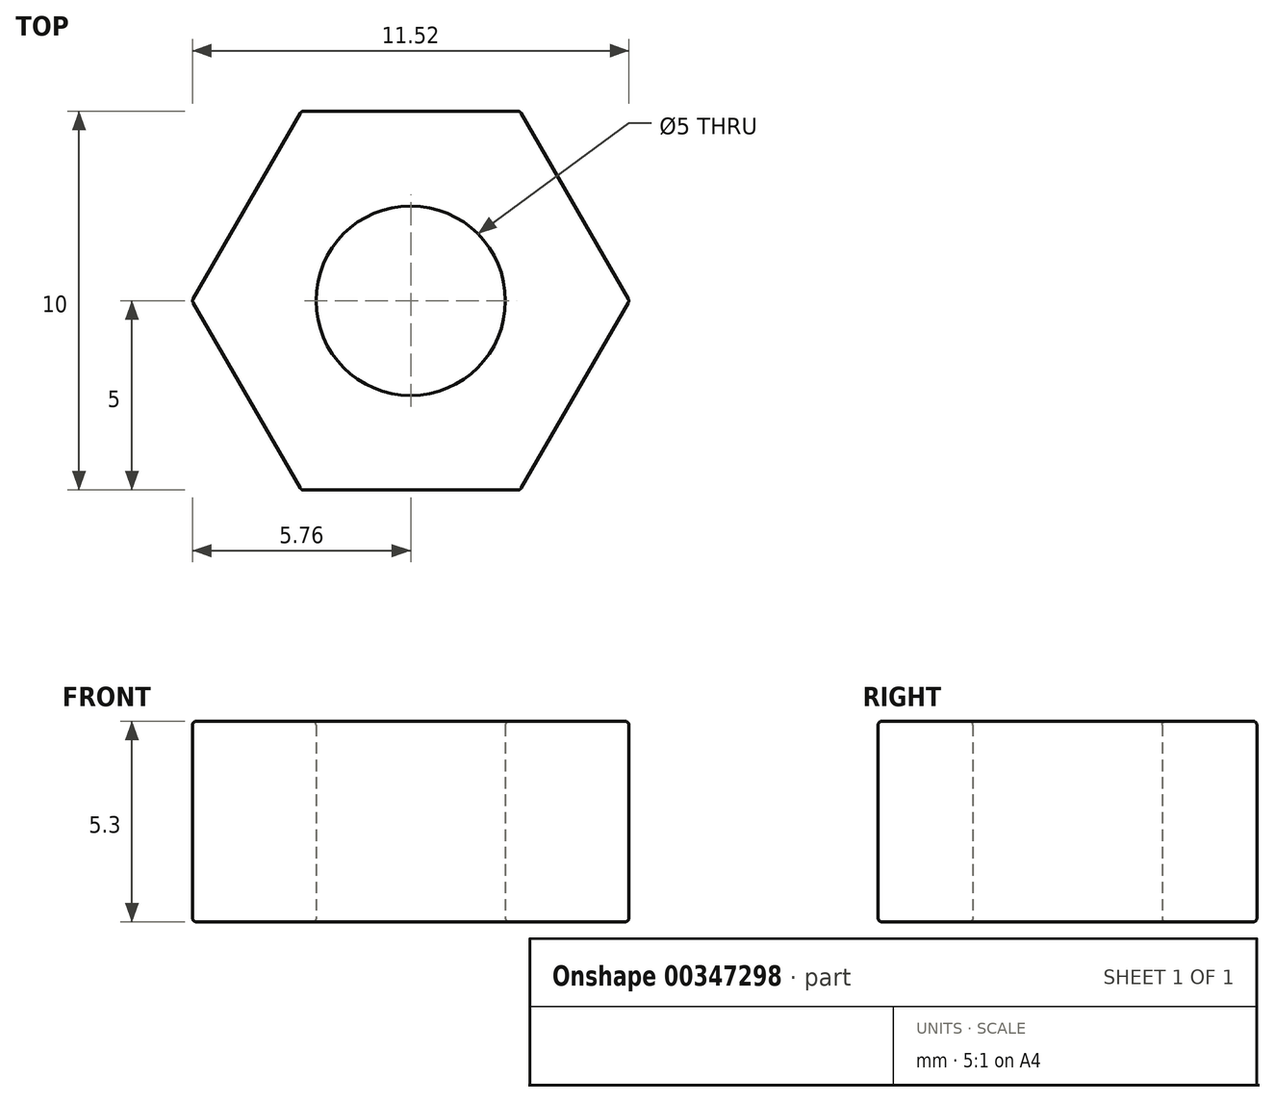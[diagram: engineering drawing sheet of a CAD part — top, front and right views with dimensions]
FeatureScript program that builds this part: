
annotation { "Feature Type Name" : "Feature", "Feature Type Description" : "" }
export const myFeature = defineFeature(function(context is Context, id is Id, definition is map)
    precondition{}
    {
        {
            var Q0;
            Q0=qCreatedBy(makeId("Top.planeOp"),FACE);
            var sketch = newSketch(context, id + "F0", { "sketchPlane" : qUnion([Q0])});
            skCircle(sketch, "E0.cCircle", {"center": v(0, 0) * mm, "radius": 5 * mm, "construction": true});
            skLineSegment(sketch, "E0.0", {"start": v(2.89, 5) * mm, "end": v(5.77, 0) * mm});
            skLineSegment(sketch, "E0.1", {"start": v(5.77, 0) * mm, "end": v(2.89, -5) * mm});
            skLineSegment(sketch, "E0.2", {"start": v(2.89, -5) * mm, "end": v(-2.89, -5) * mm});
            skLineSegment(sketch, "E0.3", {"start": v(-2.89, -5) * mm, "end": v(-5.77, 0) * mm});
            skLineSegment(sketch, "E0.4", {"start": v(-5.77, 0) * mm, "end": v(-2.89, 5) * mm});
            skLineSegment(sketch, "E0.5", {"start": v(-2.89, 5) * mm, "end": v(2.89, 5) * mm});
            skPoint(sketch, "E0.0.midPoint", {"position": v(4.33, 2.5) * mm});
            skCircle(sketch, "E1", {"center": v(0, 0) * mm, "radius": 2.5 * mm});
            skSolve(sketch);
        }
        {
            var Q0;
            Q0 = qSketchRegion(id + "F0", true);
            extrude(context, id + "F1", {"entities" : qUnion([Q0]), "depth" : 5.3 * mm});
        }
        {
            var Q0;
            Q0=makeQuery(id+"F1.opExtrude","SWEPT_FACE",FACE,{"disambiguationData":[OSD([sQuery(id+"F0.wireOp",EDGE,"E0.0")])]});
            var Q1;
            Q1=makeQuery(id+"F1.opExtrude","SWEPT_FACE",FACE,{"disambiguationData":[OSD([sQuery(id+"F0.wireOp",EDGE,"E0.1")])]});
            var Q2;
            Q2=makeQuery(id+"F1.opExtrude","CAP_FACE",FACE,{"disambiguationData":[OSD([sQuery(id+"F0.wireOp",EDGE,"E0.0"),sQuery(id+"F0.wireOp",EDGE,"E0.1"),sQuery(id+"F0.wireOp",EDGE,"E0.2"),sQuery(id+"F0.wireOp",EDGE,"E0.3"),sQuery(id+"F0.wireOp",EDGE,"E0.4"),sQuery(id+"F0.wireOp",EDGE,"E0.5"),sQuery(id+"F0.wireOp",EDGE,"E1")])],"isStart":false});
            var Q3;
            Q3=makeQuery(id+"F1.opExtrude","SWEPT_FACE",FACE,{"disambiguationData":[OSD([sQuery(id+"F0.wireOp",EDGE,"E0.2")])]});
            var Q4;
            Q4=makeQuery(id+"F1.opExtrude","CAP_FACE",FACE,{"disambiguationData":[OSD([sQuery(id+"F0.wireOp",EDGE,"E0.0"),sQuery(id+"F0.wireOp",EDGE,"E0.1"),sQuery(id+"F0.wireOp",EDGE,"E0.2"),sQuery(id+"F0.wireOp",EDGE,"E0.3"),sQuery(id+"F0.wireOp",EDGE,"E0.4"),sQuery(id+"F0.wireOp",EDGE,"E0.5"),sQuery(id+"F0.wireOp",EDGE,"E1")])],"isStart":true});
            var Q5;
            Q5=makeQuery(id+"F1.opExtrude","SWEPT_EDGE",EDGE,{"disambiguationData":[OSD([sQuery(id+"F0.wireOp",EDGE,"E0.4"),sQuery(id+"F0.wireOp",EDGE,"E0.5")])]});
            var Q6;
            Q6=makeQuery(id+"F1.opExtrude","SWEPT_FACE",FACE,{"disambiguationData":[OSD([sQuery(id+"F0.wireOp",EDGE,"E0.3")])]});
            fillet(context, id + "F2", {"entities" : qUnion([Q0, Q1, Q2, Q3, Q4, Q5, Q6]), "radius" : 0.1 * mm, "tangentPropagation" : true, "allowEdgeOverflow" : false});
        }
    });
